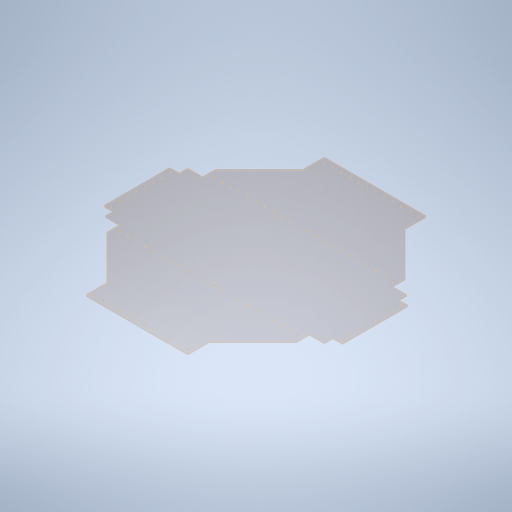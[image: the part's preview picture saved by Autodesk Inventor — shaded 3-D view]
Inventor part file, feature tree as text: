
AUTODESK INVENTOR PART (.ipt)
format: ipt  version: 2023.4 (Build 274418000, 418)  size: 506,880 bytes
history: native  units: in
note: dims shown in document units (in); Inventor stores cm internally (conversion verified against a paired STEP export)
features: sketch x4, extrude x2, hole x2, fillet x1, projected_geometry x1
ambient origin geometry x8: Origin, YZ Plane, XZ Plane, XY Plane, X Axis, Y Axis, Z Axis, Center Point
bodies: Solid1 (feature_tree)
feature tree (10):
  extrude  "Extrusion1"  Depth=28.0in
  hole  "Hole1"  [1 undecoded]
  extrude  "Extrusion2"  Depth=0.125in TaperAngle=0.0deg
  fillet  "Fillet1"  Radius=0.5in
  hole  "Hole2"  [1 undecoded]
  sketch  "Sketch1"  dims[d0=28.0in d1=28.0in]
  sketch  "Sketch2"  dims[d2=2.5in d3=8.0in]
  sketch  "Sketch3"  dims[d4=1.5748in d6=360.0deg d8=0.125in d9=0.0in d10=0.5in]
  projected_geometry  "Projected Loop1"
  sketch  "Sketch4"  dims[d11=0.5in d12=0.5in d13=0.5in d14=0.5in d15=0.5in d16=4.7244in d18=1.0in d19=0.3937in d21=1.0in d23=4.7244in d25=1.0in d26=0.3937in d28=1.0in d30=0.201in d31=0.75in d32=0.385in d33=0.25in d34=0.5635in d35=1.0in d36=0.8108in d37=0.0in d38=0.0in d39=2.125in d40=1.125in d42=1.125in d43=2.875in d44=0.13in d45=8.5in d46=8.5in d47=3.5in d48=8.6614in d50=1.0in d51=0.3937in d53=1.0in d55=0.201in d56=0.75in d57=0.375in d58=0.25in d59=0.5635in d60=1.0in d61=0.8108in]
note: 2 required parameter values undecoded (feature->parameter linkage not recoverable at this tier; creation-order binding heuristic only, values carry confidence <= 0.55)
